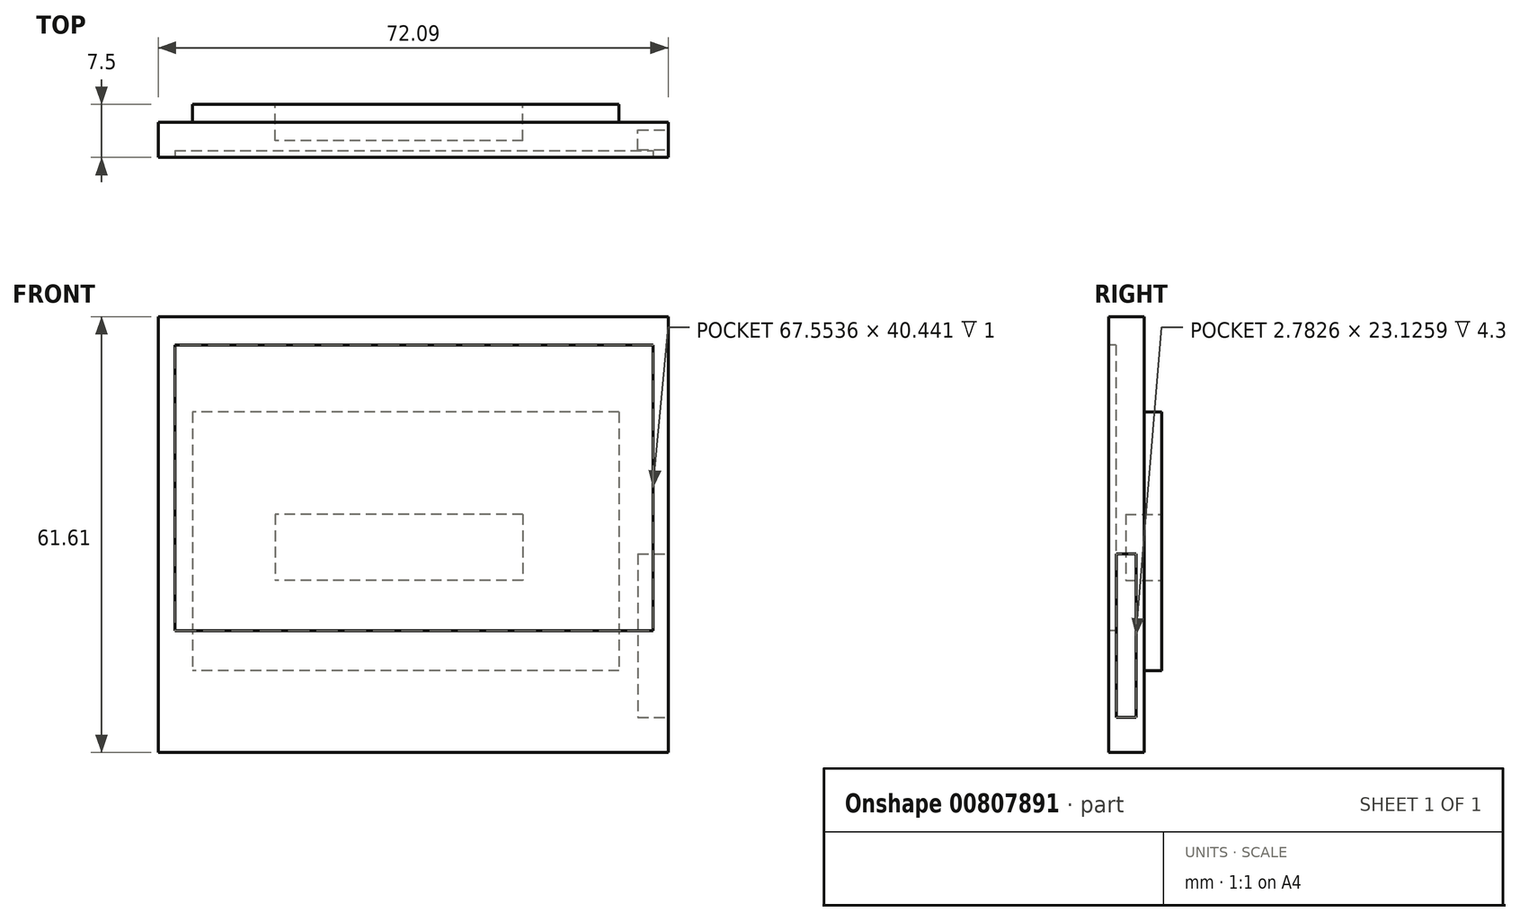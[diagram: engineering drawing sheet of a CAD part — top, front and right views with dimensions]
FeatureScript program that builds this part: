
annotation { "Feature Type Name" : "Feature", "Feature Type Description" : "" }
export const myFeature = defineFeature(function(context is Context, id is Id, definition is map)
    precondition{}
    {
        {
            var Q0;
            Q0=qCreatedBy(makeId("Front.planeOp"),FACE);
            var sketch = newSketch(context, id + "F0", { "sketchPlane" : qUnion([Q0])});
            skLineSegment(sketch, "E0.bottom", {"start": v(0, 61.61) * mm, "end": v(72.1, 61.61) * mm});
            skLineSegment(sketch, "E0.top", {"start": v(0, 0) * mm, "end": v(72.1, 0) * mm});
            skLineSegment(sketch, "E0.left", {"start": v(0, 61.61) * mm, "end": v(0, 0) * mm});
            skLineSegment(sketch, "E0.right", {"start": v(72.1, 61.61) * mm, "end": v(72.1, 0) * mm});
            skSolve(sketch);
        }
        {
            var Q0;
            Q0=makeQuery(id+"F0.imprint","IMPRINT",FACE,{"disambiguationData":[TD([[makeQuery(id+"F0.imprint","IMPRINT",EDGE,{"derivedFrom":sQuery(id+"F0.wireOp",EDGE,"E0.bottom")}),-1.0]])]});
            extrude(context, id + "F1", {"entities" : qUnion([Q0]), "depth" : 5 * mm, "offsetDistance" : 25 * mm});
        }
        {
            var Q0;
            Q0=makeQuery(id+"F1.opExtrude","CAP_FACE",FACE,{"disambiguationData":[OSD([sQuery(id+"F0.wireOp",EDGE,"E0.bottom"),sQuery(id+"F0.wireOp",EDGE,"E0.top"),sQuery(id+"F0.wireOp",EDGE,"E0.left"),sQuery(id+"F0.wireOp",EDGE,"E0.right")])],"isStart":false});
            var sketch = newSketch(context, id + "F2", { "sketchPlane" : qUnion([Q0])});
            skSolve(sketch);
        }
        {
            var Q0;
            Q0=makeQuery(id+"F2.imprint","IMPRINT",FACE,{"disambiguationData":[TD([[makeQuery(id+"F2.imprint","IMPRINT",EDGE,{"derivedFrom":makeQuery(id+"F1.opExtrude","CAP_EDGE",EDGE,{"disambiguationData":[OSD([sQuery(id+"F0.wireOp",EDGE,"E0.bottom")])],"isStart":false})}),-1.0]])]});
            var sketch = newSketch(context, id + "F3", { "sketchPlane" : qUnion([Q0])});
            skLineSegment(sketch, "E1.bottom", {"start": v(2.4, 57.61) * mm, "end": v(69.95, 57.61) * mm});
            skLineSegment(sketch, "E1.top", {"start": v(2.4, 17.17) * mm, "end": v(69.95, 17.17) * mm});
            skLineSegment(sketch, "E1.left", {"start": v(2.4, 57.61) * mm, "end": v(2.4, 17.17) * mm});
            skLineSegment(sketch, "E1.right", {"start": v(69.95, 57.61) * mm, "end": v(69.95, 17.17) * mm});
            skSolve(sketch);
        }
        {
            var Q0;
            Q0=makeQuery(id+"F3.imprint","IMPRINT",FACE,{"disambiguationData":[TD([[makeQuery(id+"F3.imprint","IMPRINT",EDGE,{"derivedFrom":sQuery(id+"F3.wireOp",EDGE,"E1.bottom")}),-1.0]])]});
            extrude(context, id + "F4", {"entities" : qUnion([Q0]), "operationType" : NewBodyOperationType.REMOVE, "oppositeDirection" : true, "depth" : 1 * mm, "offsetDistance" : 25 * mm});
        }
        {
            var Q0;
            Q0=makeQuery(id+"F1.opExtrude","CAP_FACE",FACE,{"disambiguationData":[OSD([sQuery(id+"F0.wireOp",EDGE,"E0.bottom"),sQuery(id+"F0.wireOp",EDGE,"E0.top"),sQuery(id+"F0.wireOp",EDGE,"E0.left"),sQuery(id+"F0.wireOp",EDGE,"E0.right")])],"isStart":true});
            var sketch = newSketch(context, id + "F5", { "sketchPlane" : qUnion([Q0])});
            skLineSegment(sketch, "E2.bottom", {"start": v(-65.15, 48.1) * mm, "end": v(-4.84, 48.1) * mm});
            skLineSegment(sketch, "E2.top", {"start": v(-65.15, 11.57) * mm, "end": v(-4.84, 11.57) * mm});
            skLineSegment(sketch, "E2.left", {"start": v(-65.15, 48.1) * mm, "end": v(-65.15, 11.57) * mm});
            skLineSegment(sketch, "E2.right", {"start": v(-4.84, 48.1) * mm, "end": v(-4.84, 11.57) * mm});
            skSolve(sketch);
        }
        {
            var Q0;
            Q0=makeQuery(id+"F5.imprint","IMPRINT",FACE,{"disambiguationData":[TD([[makeQuery(id+"F5.imprint","IMPRINT",EDGE,{"derivedFrom":sQuery(id+"F5.wireOp",EDGE,"E2.bottom")}),-1.0]])]});
            extrude(context, id + "F6", {"entities" : qUnion([Q0]), "operationType" : NewBodyOperationType.ADD, "depth" : 2.5 * mm, "offsetDistance" : 25 * mm});
        }
        {
            var Q0;
            Q0=makeQuery(id+"F6.opExtrude","CAP_FACE",FACE,{"disambiguationData":[OSD([sQuery(id+"F5.wireOp",EDGE,"E2.bottom"),sQuery(id+"F5.wireOp",EDGE,"E2.top"),sQuery(id+"F5.wireOp",EDGE,"E2.left"),sQuery(id+"F5.wireOp",EDGE,"E2.right")])],"isStart":false});
            var sketch = newSketch(context, id + "F7", { "sketchPlane" : qUnion([Q0])});
            skLineSegment(sketch, "E3.bottom", {"start": v(-51.55, 33.66) * mm, "end": v(-16.57, 33.66) * mm});
            skLineSegment(sketch, "E3.top", {"start": v(-51.55, 24.3) * mm, "end": v(-16.57, 24.3) * mm});
            skLineSegment(sketch, "E3.left", {"start": v(-51.55, 33.66) * mm, "end": v(-51.55, 24.3) * mm});
            skLineSegment(sketch, "E3.right", {"start": v(-16.57, 33.66) * mm, "end": v(-16.57, 24.3) * mm});
            skSolve(sketch);
        }
        {
            var Q0;
            Q0=makeQuery(id+"F7.imprint","IMPRINT",FACE,{"disambiguationData":[TD([[makeQuery(id+"F7.imprint","IMPRINT",EDGE,{"derivedFrom":sQuery(id+"F7.wireOp",EDGE,"E3.bottom")}),-1.0]])]});
            extrude(context, id + "F8", {"entities" : qUnion([Q0]), "operationType" : NewBodyOperationType.REMOVE, "oppositeDirection" : true, "depth" : 5.1 * mm, "offsetDistance" : 25 * mm});
        }
        {
            var Q0;
            Q0=makeQuery(id+"F1.opExtrude","SWEPT_FACE",FACE,{"disambiguationData":[OSD([sQuery(id+"F0.wireOp",EDGE,"E0.right")])]});
            var sketch = newSketch(context, id + "F9", { "sketchPlane" : qUnion([Q0])});
            skLineSegment(sketch, "E4.bottom", {"start": v(-3.89, 28.06) * mm, "end": v(-1.1, 28.06) * mm});
            skLineSegment(sketch, "E4.top", {"start": v(-3.89, 4.94) * mm, "end": v(-1.1, 4.94) * mm});
            skLineSegment(sketch, "E4.left", {"start": v(-3.89, 28.06) * mm, "end": v(-3.89, 4.94) * mm});
            skLineSegment(sketch, "E4.right", {"start": v(-1.1, 28.06) * mm, "end": v(-1.1, 4.94) * mm});
            skSolve(sketch);
        }
        {
            var Q0;
            Q0=makeQuery(id+"F9.imprint","IMPRINT",FACE,{"disambiguationData":[TD([[makeQuery(id+"F9.imprint","IMPRINT",EDGE,{"derivedFrom":sQuery(id+"F9.wireOp",EDGE,"E4.bottom")}),-1.0]])]});
            extrude(context, id + "F10", {"entities" : qUnion([Q0]), "operationType" : NewBodyOperationType.REMOVE, "oppositeDirection" : true, "depth" : 4.3 * mm, "offsetDistance" : 25 * mm});
        }
    });
